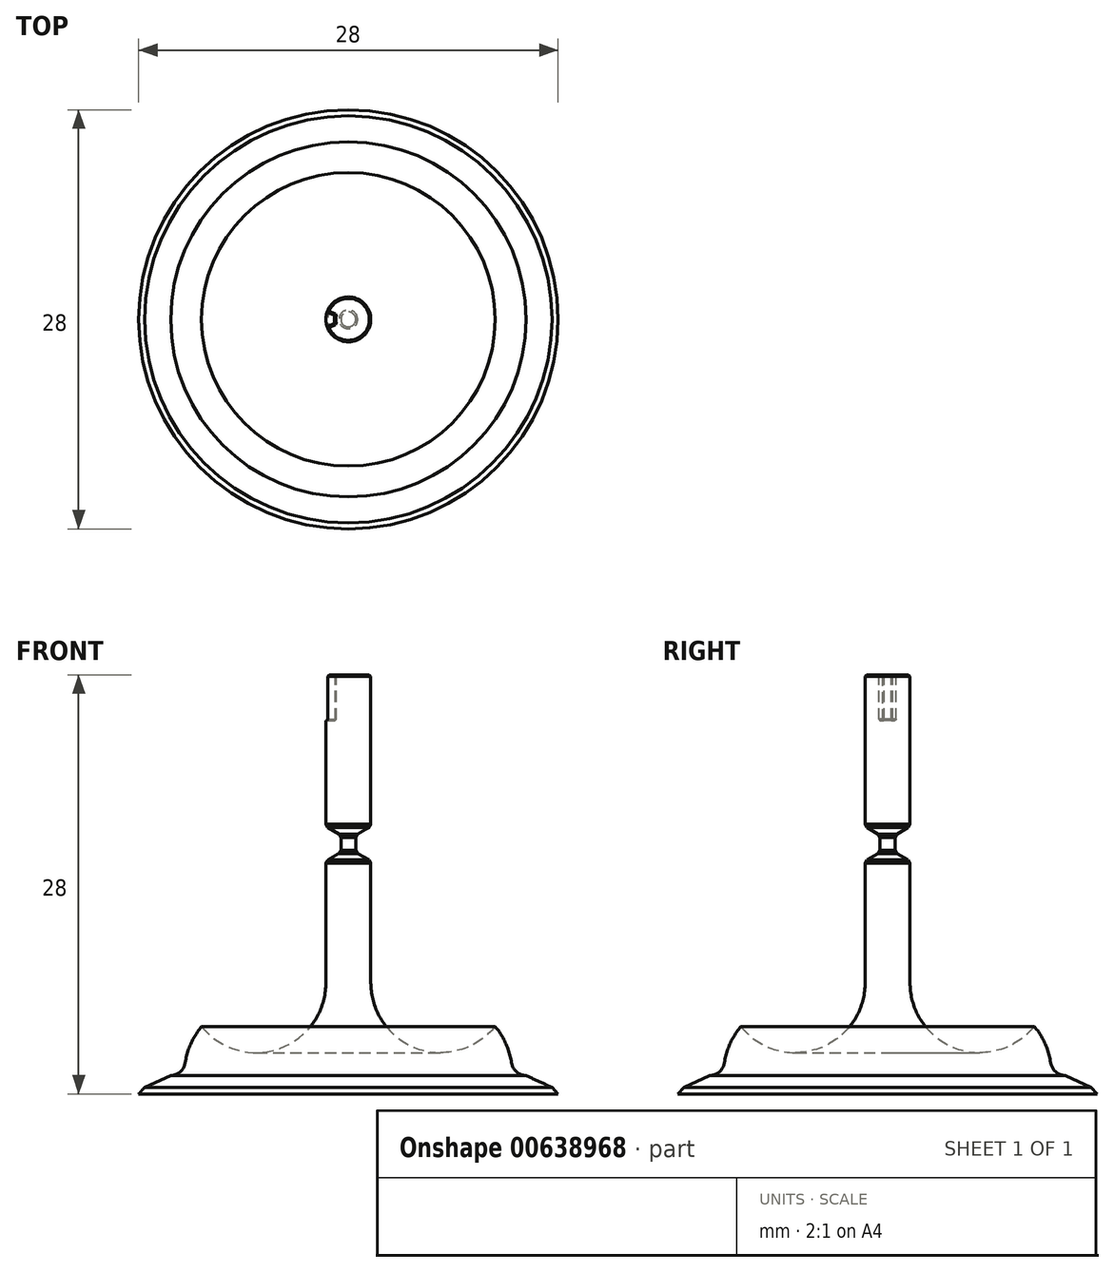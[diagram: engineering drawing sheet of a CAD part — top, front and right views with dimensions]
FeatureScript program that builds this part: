
annotation { "Feature Type Name" : "Feature", "Feature Type Description" : "" }
export const myFeature = defineFeature(function(context is Context, id is Id, definition is map)
    precondition{}
    {
        {
            var Q0;
            Q0=qCreatedBy(makeId("Front.planeOp"),FACE);
            var sketch = newSketch(context, id + "F0", { "sketchPlane" : qUnion([Q0])});
            skLineSegment(sketch, "E0", {"start": v(-14, 0) * mm, "end": v(0, 0) * mm});
            skLineSegment(sketch, "E1", {"start": v(0, 0) * mm, "end": v(0, 28) * mm});
            skLineSegment(sketch, "E2", {"start": v(-14, 0) * mm, "end": v(-12.6, 1.5) * mm});
            skLineSegment(sketch, "E3", {"start": v(-9.8, 4.5) * mm, "end": v(-1.5, 7.43) * mm, "construction": true});
            skLineSegment(sketch, "E4", {"start": v(-1.5, 7.43) * mm, "end": v(-1.5, 15.56) * mm});
            skLineSegment(sketch, "E5", {"start": v(-1.5, 28) * mm, "end": v(0, 28) * mm});
            skLineSegment(sketch, "E6", {"start": v(-1.5, 26) * mm, "end": v(-1.5, 28) * mm});
            skArc(sketch, "E7", {"start": v(-9.8, 4.5) * mm, "mid": v(-4.62, 3.02) * mm, "end": v(-1.5, 7.43) * mm});
            skLineSegment(sketch, "E8", {"start": v(-11.2, 3) * mm, "end": v(-9.8, 4.5) * mm});
            skLineSegment(sketch, "E9", {"start": v(-12.6, 1.5) * mm, "end": v(-11.2, 3) * mm, "construction": true});
            skArc(sketch, "E10", {"start": v(-12.6, 1.5) * mm, "mid": v(-11.15, 1.55) * mm, "end": v(-11.2, 3) * mm});
            skCircle(sketch, "E11.cCircle", {"center": v(-1.5, 16.71) * mm, "radius": 1 * mm, "construction": true});
            skLineSegment(sketch, "E11.0", {"start": v(-2.5, 17.29) * mm, "end": v(-1.5, 17.87) * mm, "construction": true});
            skLineSegment(sketch, "E11.1", {"start": v(-1.5, 17.87) * mm, "end": v(-0.5, 17.29) * mm});
            skLineSegment(sketch, "E11.2", {"start": v(-0.5, 17.29) * mm, "end": v(-0.5, 16.14) * mm});
            skLineSegment(sketch, "E11.3", {"start": v(-0.5, 16.14) * mm, "end": v(-1.5, 15.56) * mm});
            skLineSegment(sketch, "E11.4", {"start": v(-1.5, 15.56) * mm, "end": v(-2.5, 16.14) * mm, "construction": true});
            skLineSegment(sketch, "E11.5", {"start": v(-2.5, 16.14) * mm, "end": v(-2.5, 17.29) * mm, "construction": true});
            skPoint(sketch, "E11.0.midPoint", {"position": v(-2, 17.58) * mm});
            skLineSegment(sketch, "E12", {"start": v(-1.5, 17.87) * mm, "end": v(-1.5, 24.93) * mm});
            skLineSegment(sketch, "E13", {"start": v(-1.5, 15.56) * mm, "end": v(-1.5, 17.87) * mm, "construction": true});
            skLineSegment(sketch, "E14", {"start": v(-1.5, 28) * mm, "end": v(-0.84, 28) * mm});
            skLineSegment(sketch, "E15", {"start": v(-0.84, 28) * mm, "end": v(-0.84, 24.93) * mm});
            skLineSegment(sketch, "E16", {"start": v(-0.84, 24.93) * mm, "end": v(-1.5, 24.93) * mm});
            skLineSegment(sketch, "E17", {"start": v(-1.5, 28) * mm, "end": v(-1.5, 28) * mm});
            skLineSegment(sketch, "E18", {"start": v(-1.5, 24.93) * mm, "end": v(-1.5, 26) * mm});
            skSolve(sketch);
        }
        {
            var Q0;
            Q0=makeQuery(id+"F0.imprint","IMPRINT",FACE,{"disambiguationData":[TD([[makeQuery(id+"F0.imprint","IMPRINT",EDGE,{"derivedFrom":sQuery(id+"F0.wireOp",EDGE,"E0")}),1.0]])]});
            var Q1;
            {var subQ0=sQuery(id+"F0.wireOp",EDGE,"E6");Q1=makeQuery(id+"F0.imprint","IMPRINT",FACE,{"disambiguationData":[TD([[makeQuery(id+"F0.imprint","IMPRINT",EDGE,{"derivedFrom":subQ0}),-1.0]])]});}
            var Q2;
            Q2=sQuery(id+"F0.wireOp",EDGE,"E1");
            revolve(context, id + "F1", {"entities" : qUnion([Q0, Q1]), "axis" : qUnion([Q2]), "revolveType" : RevolveType.FULL});
        }
        {
            var Q0;
            {var subQ0=sQuery(id+"F0.wireOp",EDGE,"E6");Q0=makeQuery(id+"F0.imprint","IMPRINT",FACE,{"disambiguationData":[TD([[makeQuery(id+"F0.imprint","IMPRINT",EDGE,{"derivedFrom":subQ0}),-1.0]])]});}
            var Q1;
            Q1=sQuery(id+"F0.wireOp",EDGE,"E1");
            revolve(context, id + "F2", {"operationType" : NewBodyOperationType.REMOVE, "entities" : qUnion([Q0]), "axis" : qUnion([Q1]), "revolveType" : RevolveType.SYMMETRIC, "oppositeDirection" : true, "angle" : 45 * degree});
        }
        {
            var Q0;
            Q0=makeQuery(id+"F1.opRevolve","SWEPT_EDGE",EDGE,{"disambiguationData":[OSD([sQuery(id+"F0.wireOp",EDGE,"E8"),sQuery(id+"F0.wireOp",EDGE,"E10")])]});
            fillet(context, id + "F3", {"entities" : qUnion([Q0]), "radius" : 5 * mm, "tangentPropagation" : true, "allowEdgeOverflow" : false});
        }
        {
            var Q0;
            Q0=makeQuery(id+"F1.opRevolve","SWEPT_EDGE",EDGE,{"disambiguationData":[OSD([sQuery(id+"F0.wireOp",EDGE,"E2"),sQuery(id+"F0.wireOp",EDGE,"E10")])]});
            chamfer(context, id + "F4", {"entities" : qUnion([Q0]), "width" : 2.5 * mm, "tangentPropagation" : true});
        }
        {
            var Q0;
            Q0=makeQuery(id+"F1.opRevolve","SWEPT_FACE",FACE,{"disambiguationData":[OSD([sQuery(id+"F0.wireOp",EDGE,"E11.3")])]});
            var Q1;
            Q1=makeQuery(id+"F1.opRevolve","SWEPT_EDGE",EDGE,{"disambiguationData":[OSD([sQuery(id+"F0.wireOp",EDGE,"E11.1"),sQuery(id+"F0.wireOp",EDGE,"E11.2")])]});
            var Q2;
            Q2=makeQuery(id+"F1.opRevolve","SWEPT_EDGE",EDGE,{"disambiguationData":[OSD([sQuery(id+"F0.wireOp",EDGE,"E11.1"),sQuery(id+"F0.wireOp",EDGE,"E12")])]});
            chamfer(context, id + "F5", {"entities" : qUnion([Q0, Q1, Q2]), "width" : .25 * mm, "tangentPropagation" : true});
        }
        {
            var Q0;
            Q0=makeQuery(id+"F2.boolean.opBoolean","COPY",EDGE,{"derivedFrom":makeQuery(id+"F2.opRevolve","CAP_EDGE",EDGE,{"disambiguationData":[OSD([sQuery(id+"F0.wireOp",EDGE,"E6"),sQuery(id+"F0.wireOp",EDGE,"E18")])],"isStart":true})});
            var Q1;
            Q1=makeQuery(id+"F2.boolean.opBoolean","COPY",EDGE,{"derivedFrom":makeQuery(id+"F2.opRevolve","SWEPT_EDGE",EDGE,{"disambiguationData":[OSD([sQuery(id+"F0.wireOp",EDGE,"E12"),sQuery(id+"F0.wireOp",EDGE,"E16"),sQuery(id+"F0.wireOp",EDGE,"E18")])]})});
            var Q2;
            Q2=makeQuery(id+"F2.boolean.opBoolean","COPY",EDGE,{"derivedFrom":makeQuery(id+"F2.opRevolve","CAP_EDGE",EDGE,{"disambiguationData":[OSD([sQuery(id+"F0.wireOp",EDGE,"E6"),sQuery(id+"F0.wireOp",EDGE,"E18")])],"isStart":false})});
            var Q3;
            Q3=makeQuery(id+"F2.boolean.opBoolean","COPY",EDGE,{"derivedFrom":makeQuery(id+"F2.opRevolve","CAP_EDGE",EDGE,{"disambiguationData":[OSD([sQuery(id+"F0.wireOp",EDGE,"E14")])],"isStart":false})});
            var Q4;
            Q4=makeQuery(id+"F2.boolean.opBoolean","COPY",EDGE,{"derivedFrom":makeQuery(id+"F2.opRevolve","SWEPT_EDGE",EDGE,{"disambiguationData":[OSD([sQuery(id+"F0.wireOp",EDGE,"E5"),sQuery(id+"F0.wireOp",EDGE,"E14"),sQuery(id+"F0.wireOp",EDGE,"E15")])]})});
            var Q5;
            Q5=makeQuery(id+"F2.boolean.opBoolean","COPY",EDGE,{"derivedFrom":makeQuery(id+"F2.opRevolve","CAP_EDGE",EDGE,{"disambiguationData":[OSD([sQuery(id+"F0.wireOp",EDGE,"E14")])],"isStart":true})});
            var Q6;
            Q6=makeQuery(id+"F2.boolean.opBoolean","COPY",EDGE,{"derivedFrom":makeQuery(id+"F2.opRevolve","CAP_EDGE",EDGE,{"disambiguationData":[OSD([sQuery(id+"F0.wireOp",EDGE,"E15")])],"isStart":true})});
            var Q7;
            Q7=makeQuery(id+"F2.boolean.opBoolean","COPY",EDGE,{"derivedFrom":makeQuery(id+"F2.opRevolve","CAP_EDGE",EDGE,{"disambiguationData":[OSD([sQuery(id+"F0.wireOp",EDGE,"E16")])],"isStart":true})});
            var Q8;
            Q8=makeQuery(id+"F2.boolean.opBoolean","COPY",EDGE,{"derivedFrom":makeQuery(id+"F2.opRevolve","SWEPT_EDGE",EDGE,{"disambiguationData":[OSD([sQuery(id+"F0.wireOp",EDGE,"E15"),sQuery(id+"F0.wireOp",EDGE,"E16")])]})});
            var Q9;
            Q9=makeQuery(id+"F2.boolean.opBoolean","COPY",EDGE,{"derivedFrom":makeQuery(id+"F2.opRevolve","CAP_EDGE",EDGE,{"disambiguationData":[OSD([sQuery(id+"F0.wireOp",EDGE,"E16")])],"isStart":false})});
            var Q10;
            Q10=makeQuery(id+"F2.boolean.opBoolean","COPY",EDGE,{"derivedFrom":makeQuery(id+"F2.opRevolve","CAP_EDGE",EDGE,{"disambiguationData":[OSD([sQuery(id+"F0.wireOp",EDGE,"E15")])],"isStart":false})});
            var Q11;
            Q11=makeQuery(id+"F1.opRevolve","SWEPT_EDGE",EDGE,{"disambiguationData":[OSD([sQuery(id+"F0.wireOp",EDGE,"E6"),sQuery(id+"F0.wireOp",EDGE,"E14")])]});
            chamfer(context, id + "F6", {"entities" : qUnion([Q0, Q1, Q2, Q3, Q4, Q5, Q6, Q7, Q8, Q9, Q10, Q11]), "width" : .1 * mm, "tangentPropagation" : true});
        }
    });
